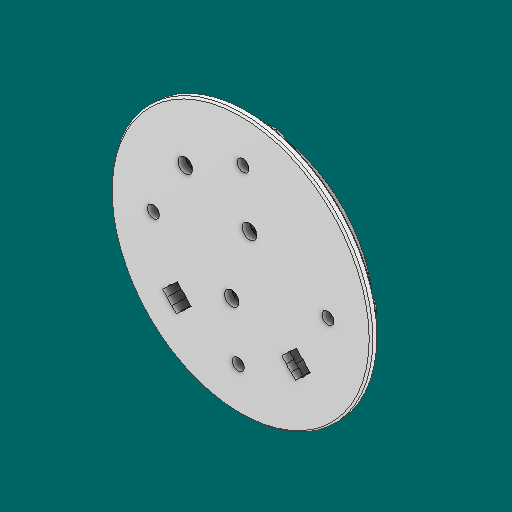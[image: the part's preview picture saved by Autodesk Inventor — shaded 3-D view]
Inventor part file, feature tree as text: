
AUTODESK INVENTOR PART (.ipt)
format: ipt  version: 2023.1 (Build 271208000, 208)  size: 637,440 bytes
history: native  units: in
note: dims shown in document units (in); Inventor stores cm internally (conversion verified against a paired STEP export)
features: sketch x6, other x3
ambient origin geometry x8: Origin, YZ Plane, XZ Plane, XY Plane, X Axis, Y Axis, Z Axis, Center Point
bodies: Solid1 (feature_tree)
feature tree (9):
  other  "SteeringCoupler_MIR.ipt"
  other  "Solid1::SteeringCoupler_MIR.ipt"
  other  "TaggingFeature1"
  sketch  "Sketch1"  dims[d0=0.3937in]
  sketch  "Sketch2"
  sketch  "Sketch4"
  sketch  "Sketch5"
  sketch  "Sketch6"
  sketch  "Sketch8"
